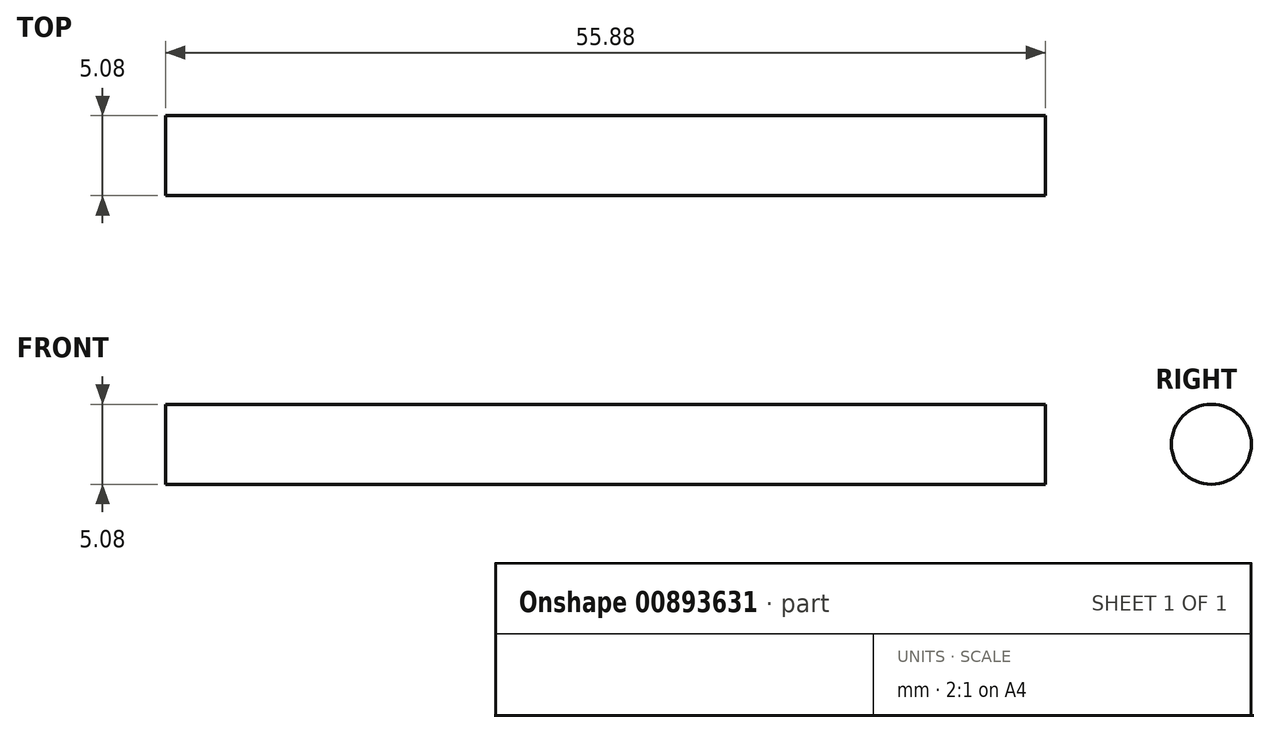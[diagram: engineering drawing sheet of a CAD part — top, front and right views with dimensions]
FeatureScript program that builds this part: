
annotation { "Feature Type Name" : "Feature", "Feature Type Description" : "" }
export const myFeature = defineFeature(function(context is Context, id is Id, definition is map)
    precondition{}
    {
        {
            var Q0;
            Q0=qCreatedBy(makeId("Right.planeOp"),FACE);
            var sketch = newSketch(context, id + "F0", { "sketchPlane" : qUnion([Q0])});
            skCircle(sketch, "E0", {"center": v(0, 0) * mm, "radius": 2.54 * mm});
            skSolve(sketch);
        }
        {
            var Q0;
            Q0=makeQuery(id+"F0.imprint","IMPRINT",FACE,{"disambiguationData":[TD([[makeQuery(id+"F0.imprint","IMPRINT",EDGE,{"derivedFrom":sQuery(id+"F0.wireOp",EDGE,"E0")}),1.0]])]});
            extrude(context, id + "F1", {"entities" : qUnion([Q0]), "depth" : 55.88 * mm, "offsetDistance" : 25.4 * mm});
        }
    });
